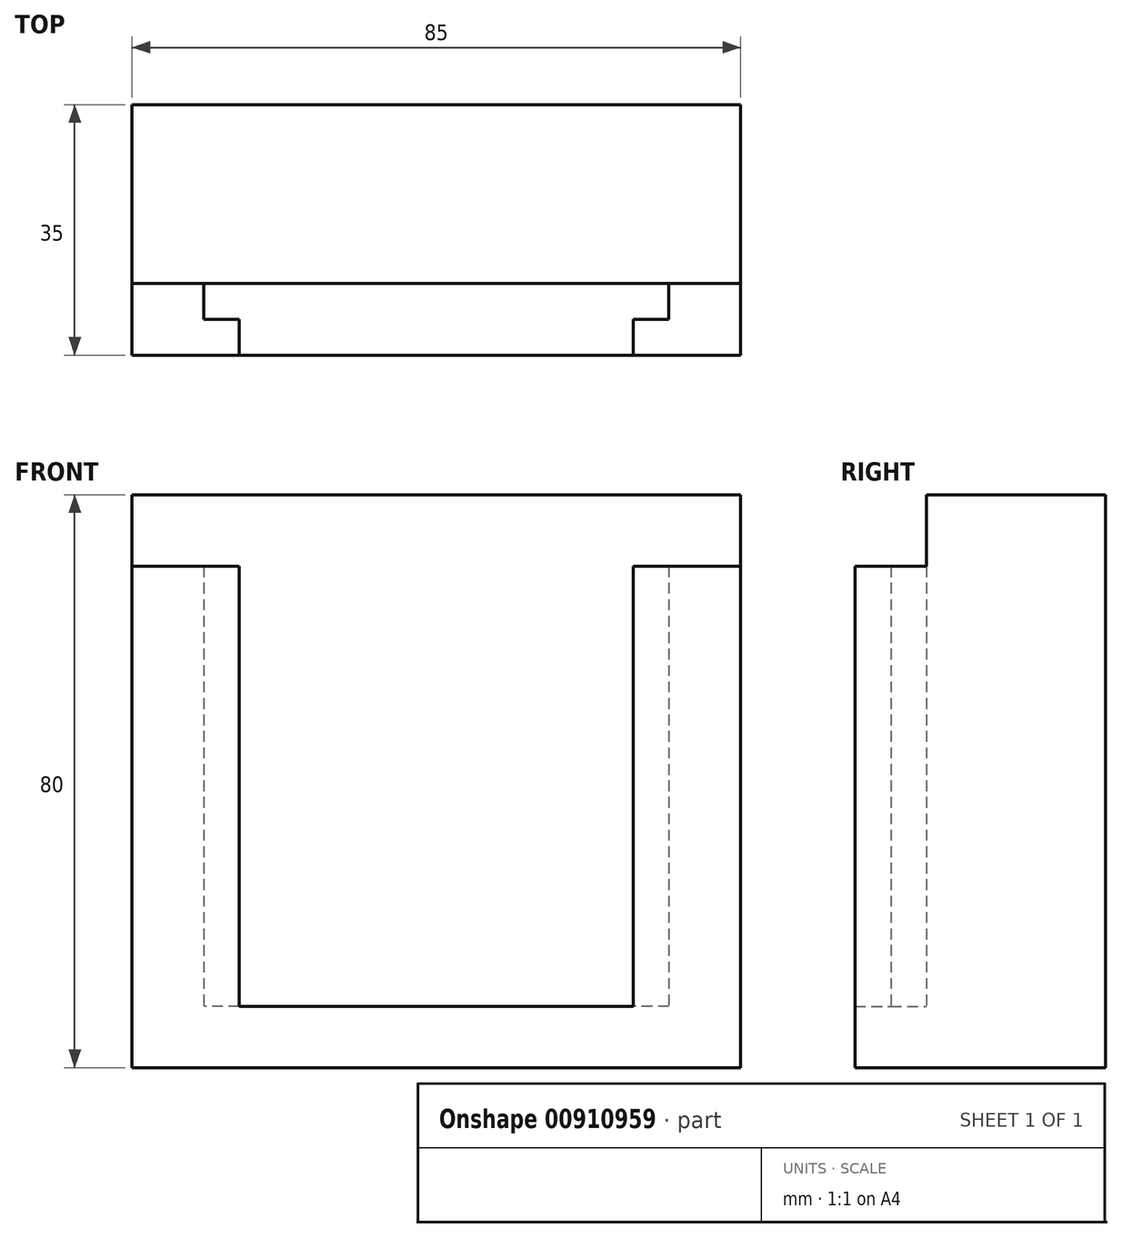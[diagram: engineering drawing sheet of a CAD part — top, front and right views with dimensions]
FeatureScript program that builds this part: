
annotation { "Feature Type Name" : "Feature", "Feature Type Description" : "" }
export const myFeature = defineFeature(function(context is Context, id is Id, definition is map)
    precondition{}
    {
        {
            var Q0;
            Q0=qCreatedBy(makeId("Front.planeOp"),FACE);
            var sketch = newSketch(context, id + "F0", { "sketchPlane" : qUnion([Q0])});
            skLineSegment(sketch, "E0", {"start": v(-40.93, 41.75) * mm, "end": v(-40.93, -38.25) * mm});
            skLineSegment(sketch, "E1", {"start": v(-40.93, -38.25) * mm, "end": v(44.07, -38.25) * mm});
            skLineSegment(sketch, "E2", {"start": v(44.07, -38.25) * mm, "end": v(44.07, 41.75) * mm});
            skLineSegment(sketch, "E3", {"start": v(44.07, 41.75) * mm, "end": v(-40.93, 41.75) * mm});
            skSolve(sketch);
        }
        {
            var Q0;
            Q0=qCreatedBy(makeId("Front.planeOp"),FACE);
            var sketch = newSketch(context, id + "F1", { "sketchPlane" : qUnion([Q0])});
            skLineSegment(sketch, "E4", {"start": v(-30.93, 31.75) * mm, "end": v(-30.93, -29.73) * mm});
            skLineSegment(sketch, "E5", {"start": v(34.07, 31.75) * mm, "end": v(34.07, -29.73) * mm});
            skLineSegment(sketch, "E6", {"start": v(34.07, -29.73) * mm, "end": v(-30.93, -29.73) * mm});
            skLineSegment(sketch, "E7", {"start": v(-30.93, 31.75) * mm, "end": v(-40.93, 31.75) * mm});
            skLineSegment(sketch, "E8", {"start": v(44.07, 31.75) * mm, "end": v(34.07, 31.75) * mm});
            skLineSegment(sketch, "E9", {"start": v(-40.93, 31.75) * mm, "end": v(-40.93, -38.25) * mm});
            skLineSegment(sketch, "E10", {"start": v(-40.93, -38.25) * mm, "end": v(44.07, -38.25) * mm});
            skLineSegment(sketch, "E11", {"start": v(44.07, -38.25) * mm, "end": v(44.07, 31.75) * mm});
            skSolve(sketch);
        }
        {
            var Q0;
            Q0=makeQuery(id+"F0.imprint","IMPRINT",FACE,{"disambiguationData":[TD([[makeQuery(id+"F0.imprint","IMPRINT",EDGE,{"derivedFrom":sQuery(id+"F0.wireOp",EDGE,"E0")}),1.0]])]});
            extrude(context, id + "F2", {"entities" : qUnion([Q0]), "oppositeDirection" : true, "depth" : 25 * mm, "offsetDistance" : 25 * mm});
        }
        {
            var Q0;
            Q0=makeQuery(id+"F1.imprint","IMPRINT",FACE,{"disambiguationData":[TD([[makeQuery(id+"F1.imprint","IMPRINT",EDGE,{"derivedFrom":sQuery(id+"F1.wireOp",EDGE,"E4")}),-1.0]])]});
            extrude(context, id + "F3", {"entities" : qUnion([Q0]), "operationType" : NewBodyOperationType.ADD, "depth" : 5 * mm, "offsetDistance" : 25 * mm});
        }
        {
            var Q0;
            Q0=makeQuery(id+"F3.opExtrude","CAP_FACE",FACE,{"disambiguationData":[OSD([sQuery(id+"F1.wireOp",EDGE,"E4"),sQuery(id+"F1.wireOp",EDGE,"E5"),sQuery(id+"F1.wireOp",EDGE,"E6"),sQuery(id+"F1.wireOp",EDGE,"E7"),sQuery(id+"F1.wireOp",EDGE,"E8"),sQuery(id+"F1.wireOp",EDGE,"E9"),sQuery(id+"F1.wireOp",EDGE,"E10"),sQuery(id+"F1.wireOp",EDGE,"E11")])],"isStart":false});
            var sketch = newSketch(context, id + "F4", { "sketchPlane" : qUnion([Q0])});
            skLineSegment(sketch, "E12", {"start": v(-40.93, 31.75) * mm, "end": v(-25.93, 31.75) * mm});
            skLineSegment(sketch, "E13", {"start": v(-25.93, 31.75) * mm, "end": v(-25.93, -29.73) * mm});
            skLineSegment(sketch, "E14", {"start": v(-25.93, -29.73) * mm, "end": v(29.07, -29.73) * mm});
            skLineSegment(sketch, "E15", {"start": v(29.07, -29.73) * mm, "end": v(29.07, 31.75) * mm});
            skLineSegment(sketch, "E16", {"start": v(29.07, 31.75) * mm, "end": v(44.07, 31.75) * mm});
            skLineSegment(sketch, "E17", {"start": v(44.07, 31.75) * mm, "end": v(44.07, -38.25) * mm});
            skLineSegment(sketch, "E18", {"start": v(44.07, -38.25) * mm, "end": v(-40.93, -38.25) * mm});
            skLineSegment(sketch, "E19", {"start": v(-40.93, -38.25) * mm, "end": v(-40.93, 31.75) * mm});
            skSolve(sketch);
        }
        {
            var Q0;
            {var subQ2=sQuery(id+"F4.wireOp",EDGE,"E13");Q0=makeQuery(id+"F4.imprint","IMPRINT",FACE,{"disambiguationData":[TD([[makeQuery(id+"F4.imprint","IMPRINT",EDGE,{"derivedFrom":subQ2}),-1.0]])]});}
            var Q1;
            {var subQ1=sQuery(id+"F4.wireOp",EDGE,"E14");Q1=makeQuery(id+"F4.imprint","IMPRINT",FACE,{"disambiguationData":[TD([[makeQuery(id+"F4.imprint","IMPRINT",EDGE,{"derivedFrom":subQ1}),1.0]])]});}
            var Q2;
            {var subQ0=sQuery(id+"F4.wireOp",EDGE,"E15");Q2=makeQuery(id+"F4.imprint","IMPRINT",FACE,{"disambiguationData":[TD([[makeQuery(id+"F4.imprint","IMPRINT",EDGE,{"derivedFrom":subQ0}),-1.0]])]});}
            extrude(context, id + "F5", {"entities" : qUnion([Q0, Q1, Q2]), "operationType" : NewBodyOperationType.ADD, "depth" : 5 * mm, "offsetDistance" : 25 * mm});
        }
    });
